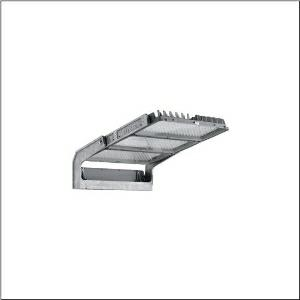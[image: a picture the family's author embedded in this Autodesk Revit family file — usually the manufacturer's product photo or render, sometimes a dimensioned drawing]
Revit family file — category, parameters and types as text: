
# Revit family: floodlight_fl_11_maxi_pro___rs12_5xa779124m01ab_02ca
name_source: partatom
category: Lighting Fixtures
units: mm (PartAtom-declared; Revit-internal decimal feet)

## family parameters
Cut with Voids When Loaded = No
Host = Face
Light Source = No
Part Type = Normal
Room Calculation Point = No
Round Connector Dimension = Use Diameter
Shared = No

## types (1)
- --- (1 x LED, 156610 lm, 1633.1 W, 5700K)
    Apparent Load = 1633 VA
    CIE Flux Codes = 79 92 99 100 100
    Color Rendering = 90
    Color Temperature = 5700K
    Default Elevation = 1800 mm
    Description = Floodlight FL 11  maxi  pro floodlight; light control with lens of PMMA; cover panel of toughened safety glass, transparent; light distribution: RS12, rotationally symmetric direct distribution, LED; colour temperature: 5700K, rated luminous flux: 156.610lm, colour rendering: CRI > 90, light colour: 957; luminous efficacy: 96lm/W; brightness control: DALI 2; with terminal, 5-pole, max. 2.5mm², mains connection: 220..240V/380..400V AC, 50/60Hz, surge voltage resistance: line to ground: 10kV, service life up to 100,000h L90. Typical operating time: 1000h per year, ECG replaceable separately, LED unit replaceable without ESD environment, dustproof LED module, dimming range 10..100%; 1633W floodlight with 3x LED unit of diecast aluminium, coated grey; length: 1.003mm / width: 651mm / height: 338mm; mounting bracket, of diecast aluminium, uncoated, natural, equipment: Power, protection rating (complete): IP66; insulation class (complete): insulation class I (protective earthing); certification: CE, ENEC, VDE; ball protection: ball impact resistant, only for outdoor installations in the designated locations, permissible operating ambient temperature: -40..+55°C, permissible storage temperature: -40..+85°Cpackaging unit: 1 piece

Light Distribution: RS12
    Height = 320 mm
    Lamp = 1 x LED
    Lamp Light Flux = 156610 lm
    Lamp Power = 1633.1 W
    Lamp count = 1
    Length = 1002 mm
    Luminous efficacy = 96 lm/W
    Manufacturer = Siteco
    ModVariant = No
    Model = 5XA779124M01AB
    Mounting Place = Ceiling
    Mounting Type = Surface mounted
    Number of Poles = 1
    OnlyDefault = Yes
    Power Factor = 1
    Product Name = Floodlight FL 11 maxi pro | RS12
    Product group = floodlight | ceiling mounted
    ProductGroupID = 302
    Protection Class = Protection class I
    Protection Degree = IP 66
    RLX_Detail_Level = 1
    RLX_Emergency_Light_Flux = 0 lm
    RLX_Emergency_Type = 0
    RLX_Emergency_Type_DB = No
    RlxData = <blob elided: 40345 chars, md5=4520bb20>
    Socket = socket
    Standby Power = 0 W
    System Light Flux = 156610 lm
    System Power = 1633 W
    Type Comments = factory setting: luminous flux: 100 % | dim-lin: 254 | 1100 mA
    Type Image = l_1356210.jpg
    URL = http://relux.com
    VarID = @adj_044423
    Voltage = 0 V
    Weight = 0.00 kg
    Width = 655 mm

## geometry (parser evidence)
native form markers: Blend x4, Sweep x12
no freeform markers — native parametric forms only
